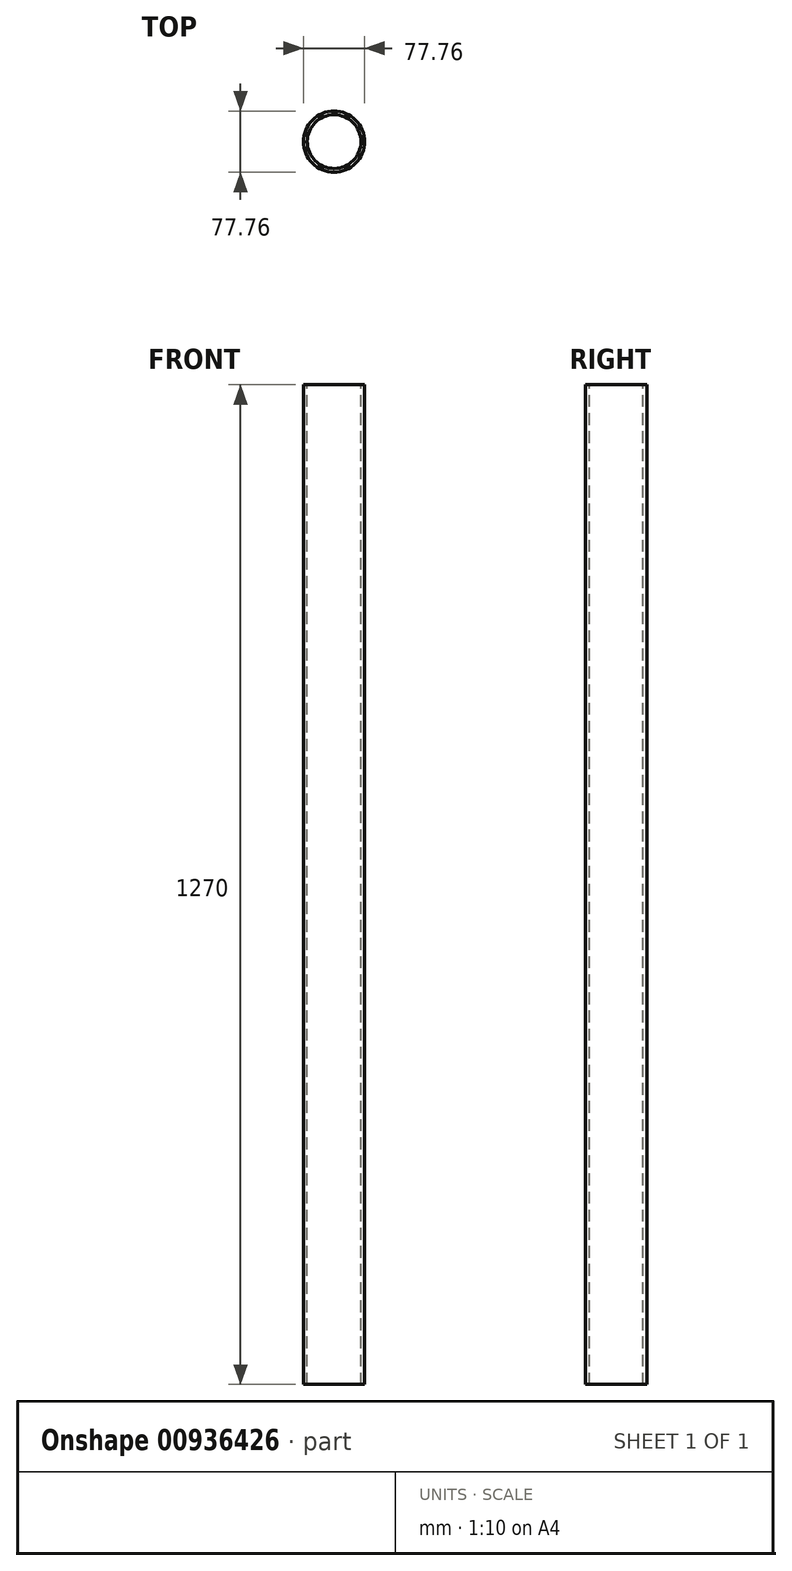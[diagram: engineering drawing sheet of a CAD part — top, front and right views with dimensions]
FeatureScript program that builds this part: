
annotation { "Feature Type Name" : "Feature", "Feature Type Description" : "" }
export const myFeature = defineFeature(function(context is Context, id is Id, definition is map)
    precondition{}
    {
        {
            var Q0;
            Q0=qCreatedBy(makeId("Top.planeOp"),FACE);
            var sketch = newSketch(context, id + "F0", { "sketchPlane" : qUnion([Q0])});
            skCircle(sketch, "E0", {"center": v(0, 0) * mm, "radius": 38.88 * mm});
            skSolve(sketch);
        }
        {
            var Q0;
            Q0=qCreatedBy(makeId("Top.planeOp"),FACE);
            var sketch = newSketch(context, id + "F1", { "sketchPlane" : qUnion([Q0])});
            skCircle(sketch, "E1", {"center": v(0, 0) * mm, "radius": 34.12 * mm});
            skSolve(sketch);
        }
        {
            var Q0;
            Q0=makeQuery(id+"F0.imprint","IMPRINT",FACE,{"disambiguationData":[TD([[makeQuery(id+"F0.imprint","IMPRINT",EDGE,{"derivedFrom":sQuery(id+"F0.wireOp",EDGE,"E0")}),1.0]])]});
            var Q1;
            Q1=makeQuery(id+"F1.imprint","IMPRINT",FACE,{"disambiguationData":[TD([[makeQuery(id+"F1.imprint","IMPRINT",EDGE,{"derivedFrom":sQuery(id+"F1.wireOp",EDGE,"E1")}),1.0]])]});
            var Q2;
            Q2=sQuery(id+"F1.wireOp",EDGE,"E1");
            var Q3;
            Q3=sQuery(id+"F0.wireOp",EDGE,"E0");
            extrude(context, id + "F2", {"entities" : qUnion([Q0, Q1]), "bodyType" : ToolBodyType.SURFACE, "surfaceEntities" : qUnion([Q2, Q3]), "depth" : 1270 * mm, "offsetDistance" : 25.4 * mm, "hasDraft" : true, "draftAngle" : 3 * degree});
        }
    });
